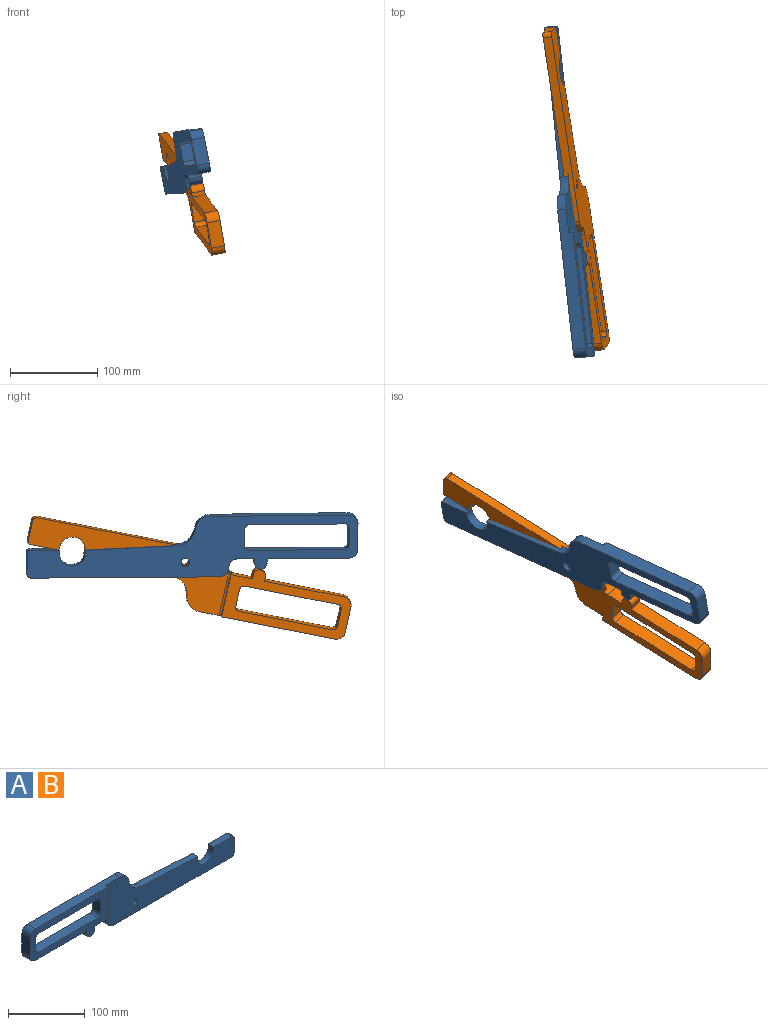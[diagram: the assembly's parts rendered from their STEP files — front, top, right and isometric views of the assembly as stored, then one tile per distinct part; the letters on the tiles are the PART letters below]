
ASSEMBLY  parts=2 mates=1
PART A: 41 faces, bbox 380.1x15x70.7 mm
  f0: plane 51.53x5mm, normal (1,0,0), area 129.1mm2, adj f1,f16,f25,f34,f37,f39
  f1: plane 236.75x70.7mm, normal (0,-1,0), area 8872.2mm2, adj f0,f2,f3,f4,f5,f6,f7,f8
  f2: plane 10x3.27mm, normal (1,0,0), area 32.7mm2, adj f1,f3,f15,f35
  f3: plane 105.46x10mm, normal (0.04,0,1), area 1055.6mm2, adj f1,f2,f4,f35
  f4: cylinder r=22mm len=20.47mm, axis (0,1,0), area 294.5mm2, adj f1,f3,f5,f35
  f5: cylinder r=17.04mm len=17.01mm, axis (0,1,0), area 257.8mm2, adj f1,f4,f16,f35
  f6: plane 10x0.7mm, normal (-1,0,0), area 7mm2, adj f1,f7,f25,f35
  f7: cylinder r=10mm len=10mm, axis (0,1,0), area 157.1mm2, adj f1,f6,f8,f35
  f8: plane 217.06x10mm, normal (0,0,-1), area 2170.6mm2, adj f1,f7,f9,f35
  f9: cylinder r=5mm len=10mm, axis (0,1,0), area 78.5mm2, adj f1,f8,f10,f35
  f10: plane 24x10mm, normal (1,0,0), area 240mm2, adj f1,f9,f11,f35
  f11: cylinder r=3mm len=10mm, axis (0,1,0), area 47.1mm2, adj f1,f10,f12,f35
  f12: plane 34.13x10mm, normal (0,0,1), area 341.3mm2, adj f1,f11,f13,f35
  f13: plane 10x3.25mm, normal (-1,0,0), area 32.5mm2, adj f1,f12,f15,f35
  f14: cylinder r=5mm len=10mm, axis (0,1,0), area 314.2mm2, adj f1,f35
  f15: cylinder r=15mm len=30mm, axis (0,1,0), area 471.2mm2, adj f1,f2,f13,f35
  f16: plane 160x15mm, normal (0,0,1), area 2266.6mm2, adj f0,f1,f5,f17,f34,f35
  f17: cylinder r=10mm len=15mm, axis (0,1,0), area 235.6mm2, adj f16,f18,f34,f35
  f18: plane 30x15mm, normal (-1,0,0), area 450mm2, adj f17,f19,f34,f35
  f19: cylinder r=10mm len=15mm, axis (0,1,0), area 235.6mm2, adj f18,f20,f34,f35
  f20: plane 94x15mm, normal (0,0,-1), area 1410mm2, adj f19,f21,f34,f35
  f21: plane 15x5mm, normal (-1,0,0), area 75mm2, adj f20,f22,f34,f35
  f22: cylinder r=7mm len=15mm, axis (0,1,0), area 329.9mm2, adj f21,f23,f34,f35
  f23: plane 15x5mm, normal (1,0,0), area 75mm2, adj f22,f24,f34,f35
  f24: plane 20x15mm, normal (0,0,-1), area 300mm2, adj f23,f25,f34,f35
  f25: cylinder r=10mm len=15mm, axis (0,1,0), area 185.1mm2, adj f0,f1,f6,f24,f34,f35,f36,f38
  f26: cylinder r=5mm len=15mm, axis (0,1,0), area 117.8mm2, adj f27,f33,f34,f35
  f27: plane 20x15mm, normal (1,0,0), area 300mm2, adj f26,f28,f34,f35
  f28: cylinder r=5mm len=15mm, axis (0,1,0), area 117.8mm2, adj f27,f29,f34,f35
  f29: plane 110x15mm, normal (0,0,-1), area 1650mm2, adj f28,f30,f34,f35
  f30: cylinder r=5mm len=15mm, axis (0,1,0), area 117.8mm2, adj f29,f31,f34,f35
  f31: plane 20x15mm, normal (-1,0,0), area 300mm2, adj f30,f32,f34,f35
  f32: cylinder r=5mm len=15mm, axis (0,1,0), area 117.8mm2, adj f31,f33,f34,f35
  f33: plane 110x15mm, normal (0,0,1), area 1650mm2, adj f26,f32,f34,f35
  f34: plane 143.31x62mm, normal (0,-1,0), area 3693.7mm2, adj f0,f16,f17,f18,f19,f20,f21,f22
  f35: plane 380.06x70.7mm, normal (0,1,0), area 12695.1mm2, adj f2,f3,f4,f5,f6,f7,f8,f9
  f36: plane 0.41x0.27mm, normal (0,1,0), area 0.1mm2, adj f25,f38,f40
  f37: cylinder r=2.5mm len=51.7mm, axis (0,0,-1), area 203mm2, adj f0,f1,f38,f39,f40
  f38: plane 2.5x0.27mm, normal (-1,0,0), area 0.7mm2, adj f25,f36,f37,f40
  f39: plane 2.5x2.5mm, normal (0,0,1), area 1.3mm2, adj f0,f1,f37
  f40: plane 2.5x2.5mm, normal (0,0,-1), area 1.3mm2, adj f1,f36,f37,f38
PART B: same geometry as A
PLACE A rot(axis=(-0.09,-0.09,0.99),96.8deg) t=(200.93,-765.95,-392.81)mm
PLACE B rot(axis=(-0.65,-0.74,-0.14),179.1deg) t=(221.03,-760.84,-419.45)mm
MATE revolute B.f14 <-> A.f14  axis (-0.98,-0.11,-0.19) through (205.68,-741.71,-404.56)mm
